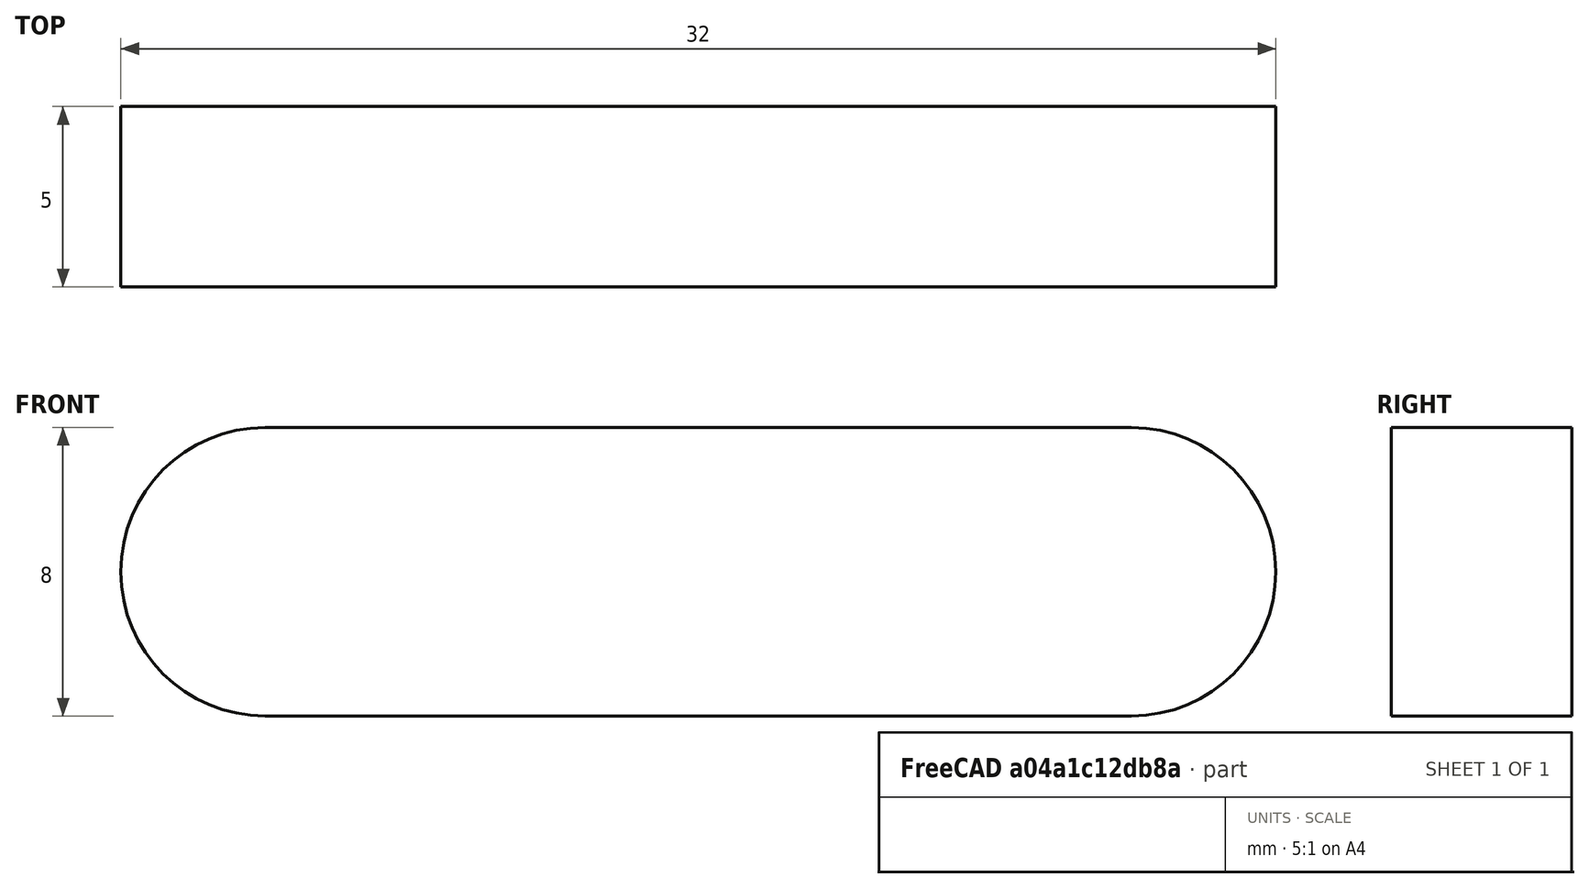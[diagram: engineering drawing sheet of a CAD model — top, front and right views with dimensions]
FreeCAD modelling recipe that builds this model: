
FCSTD DOCUMENT  (FreeCAD 0.18.4R)
Label: pulley-bars
License: All rights reserved
LicenseURL: http://en.wikipedia.org/wiki/All_rights_reserved
objects: Sketcher::SketchObject×1, PartDesign::Pad×1, PartDesign::Body×1
note: 4 computed .brp shape members not serialized (recipe doc carries the construction recipe); baked Part::Feature solids carry a one-line shape summary decoded from their .brp

FEATURE [Sketcher::SketchObject] Sketch
  MapMode = 5
  Placement = pos=(0,0,0) rot=(1,0,0;1.5708rad)
  Support = -> [XZ_Plane]
  sketch-geometry (4):
    g0: ArcOfCircle CenterX=0 CenterY=0 CenterZ=0 NormalX=0 NormalY=0 NormalZ=1 AngleXU=0 Radius=4 StartAngle=1.5708 EndAngle=4.71239
    g1: ArcOfCircle CenterX=24 CenterY=0 CenterZ=0 NormalX=0 NormalY=0 NormalZ=1 AngleXU=0 Radius=4 StartAngle=4.71239 EndAngle=7.85398
    g2: LineSegment StartX=24 StartY=4 StartZ=0 EndX=-4.90053e-06 EndY=4 EndZ=0
    g3: LineSegment StartX=-4.6118e-06 StartY=-4 StartZ=0 EndX=24 EndY=-4 EndZ=0
  constraints (14):
    c: PointOnObject(g0,g-1)
    c: PointOnObject(g1,g-1)
    c: Coincident(g2,g1)
    c: Coincident(g2,g0)
    c: Horizontal(g2)
    c: Coincident(g3,g0)
    c: Coincident(g3,g1)
    c: Horizontal(g3)
    c: Tangent(g3,g0)
    c: DistanceX(g2,g2) = 24
    c: Equal(g3,g2)
    c: Equal(g1,g0)
    c: DistanceY(g0,g0) = 8
    c: DistanceX(g0,g-1) = 0
FEATURE [PartDesign::Pad] Pad
  Length = 5
  Length2 = 100
  Placement = pos=(0,0,0) rot=(1,0,0;1.5708rad)
  Profile = -> Sketch
  Type = 0
FEATURE [PartDesign::Body] Body
  Group = -> [Sketch,Pad]
  Origin = -> Origin
  Tip = -> Pad
